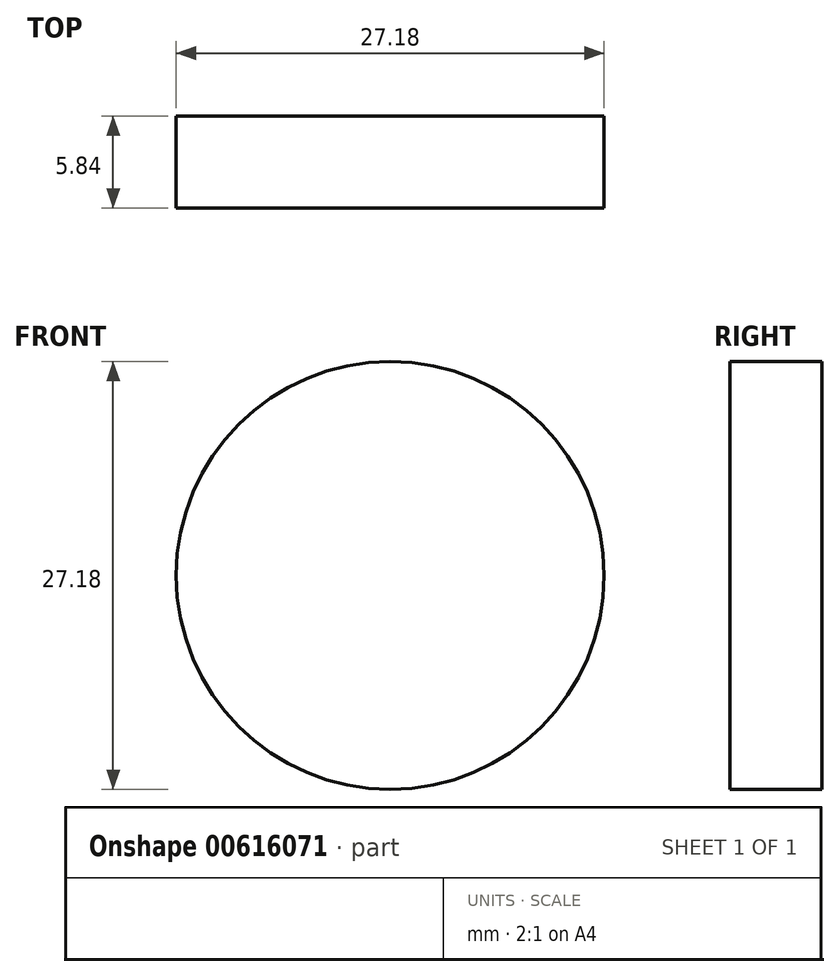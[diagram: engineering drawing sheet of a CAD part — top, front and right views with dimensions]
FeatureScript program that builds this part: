
annotation { "Feature Type Name" : "Feature", "Feature Type Description" : "" }
export const myFeature = defineFeature(function(context is Context, id is Id, definition is map)
    precondition{}
    {
        {
            var Q0;
            Q0=qCreatedBy(makeId("Front.planeOp"),FACE);
            var sketch = newSketch(context, id + "F0", { "sketchPlane" : qUnion([Q0])});
            skCircle(sketch, "E0", {"center": v(0, 0) * mm, "radius": 15.88 * mm});
            skCircle(sketch, "E1", {"center": v(0, 0) * mm, "radius": 13.59 * mm});
            skArc(sketch, "E2", {"start": v(-14.88, -5.52) * mm, "mid": v(-14.78, -2.93) * mm, "end": v(-15.86, -0.58) * mm});
            skSolve(sketch);
        }
        {
            var Q0;
            Q0=makeQuery(id+"F0.imprint","IMPRINT",FACE,{"disambiguationData":[TD([[makeQuery(id+"F0.imprint","IMPRINT",EDGE,{"derivedFrom":sQuery(id+"F0.wireOp",EDGE,"E1")}),1.0]])]});
            extrude(context, id + "F1", {"entities" : qUnion([Q0]), "depth" : 5.84 * mm, "offsetDistance" : 25.4 * mm});
        }
    });
